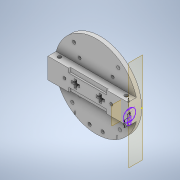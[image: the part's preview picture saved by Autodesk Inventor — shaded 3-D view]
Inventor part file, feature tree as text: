
AUTODESK INVENTOR PART (.ipt)
format: ipt  version: 2021 (Build 250183000, 183)  size: 337,920 bytes
history: native  units: mm
features: sketch x16, extrude x13, direct_edit x11, other x11, reference x9, move_body x8, plane x3, fillet x2, mirror x2
ambient origin geometry x8: Origin, YZ Plane, XZ Plane, XY Plane, X Axis, Y Axis, Z Axis, Center Point
bodies: Solid1 (feature_tree)
feature tree (75):
  sketch  "Sketch1"  dims[d0=100.0mm d1=5.0mm d2=0.0mm]
  extrude  "Extrusion1"  Depth=5.0mm TaperAngle=0.0deg
  extrude  "Extrusion2"  Depth=5.0mm
  extrude  "Extrusion3"  Depth=2.0mm
  fillet  "Fillet1"  Radius=2.0mm
  fillet  "Fillet2"  Radius=10.0mm
  extrude  "Extrusion4"  Depth=3.0mm
  extrude  "Extrusion5"  Depth=10.0mm TaperAngle=0.0deg
  plane  "Work Plane1"
  sketch  "Sketch8"  dims[d23=10.0mm d24=3.0mm]
  plane  "Work Plane3"
  extrude  "Extrusion7"  Depth=10.0mm
  plane  "Work Plane2"
  sketch  "Sketch10"  dims[d29=4.0mm d30=8.0mm]
  extrude  "Extrusion9"  Depth=3.0mm
  extrude  "Extrusion10"  Depth=3.0mm
  mirror  "Mirror3"
  extrude  "Extrusion11"  Depth=8.0mm
  extrude  "Extrusion12"  Depth=3.0mm
  extrude  "Extrusion13"  Depth=8.0mm
  direct_edit  "Direct Edit1"
  direct_edit  "Direct Edit2"
  direct_edit  "Direct Edit3"
  direct_edit  "Direct Edit4"
  direct_edit  "Direct Edit5"
  extrude  "Extrusion14"  Depth=51.75mm TaperAngle=0.0deg
  extrude  "Extrusion15"  Depth=7.0mm
  mirror  "Mirror4"
  direct_edit  "Direct Edit6"
  direct_edit  "Direct Edit7"
  direct_edit  "Direct Edit8"
  direct_edit  "Direct Edit9"
  direct_edit  "Direct Edit10"
  direct_edit  "Direct Edit11"
  sketch  "Sketch2"  dims[d3=5.0mm d4=0.0mm d5=78.0mm]
  sketch  "Sketch3"  dims[d6=3.0mm d7=0.0mm d8=2.0mm d9=2.0mm d12=10.0mm d13=0.0mm]
  reference  "Reference1"
  reference  "Reference2"
  reference  "Reference3"
  reference  "Reference4"
  sketch  "Sketch4"  dims[d15=15.0mm d17=3.0mm]
  reference  "Reference5"
  sketch  "Sketch5"  dims[d18=10.0mm d19=10.0mm d20=0.0mm]
  sketch  "Sketch6"  dims[d21=3.0mm d22=10.0mm]
  sketch  "Sketch9"  dims[d25=10.0mm d26=3.0mm]
  sketch  "Sketch11"  dims[d33=3.0mm d34=0.0mm d35=4.0mm]
  reference  "Reference6"
  reference  "Reference7"
  reference  "Reference8"
  reference  "Reference9"
  sketch  "Sketch12"  dims[d38=10.0mm d39=0.0mm d40=8.0mm]
  sketch  "Sketch13"  dims[d41=3.2mm d42=51.75mm d43=0.0mm]
  sketch  "Sketch14"  dims[d44=30.75mm d45=0.0mm d46=7.0mm]
  sketch  "Sketch15"  dims[d47=1.0mm]
  sketch  "Sketch16"  dims[d48=9.0mm]
  sketch  "Sketch17"  dims[d49=1.0mm d50=9.0mm d51=30.75mm d52=0.0mm d53=10.0mm d54=0.0mm d55=0.0mm d56=0.0mm d57=-40.0mm d58=0.0mm d59=0.0mm d60=4.75mm d61=-32.5mm d62=0.0mm d63=0.0mm d64=2.0mm d65=-2.0mm d66=5.0mm d67=5.0mm d68=2.0mm d69=0.0mm d70=85.0mm d71=33.0mm d72=4.0mm d73=4.0mm d74=28.0mm d75=0.0mm d76=0.0mm d77=1.5mm d78=0.0mm d79=0.0mm d80=1.0mm d81=0.0mm d82=-0.5mm d83=-0.5mm d84=0.0mm d85=-2.0mm d86=0.0mm d87=-2.0mm d88=0.0mm d89=0.0mm d90=2.0mm d91=0.0mm d92=0.0mm]
  parser-record x1  (decoder bookkeeping rows leaked as tree rows — omitted from the tree; the rows remain in map.json)
  other  "whole_assembly.iam"
  other  "539636 HGP-16-A-B-SSK---(asm_0_-ZH):1"
  other  "gripper extension:1"
  other  "Part3:1"
  move_body  "Move1"
  move_body  "Move2"
  move_body  "Move3"
  other  "Size1"
  other  "Delete1"
  other  "Size2"
  move_body  "Move4"
  move_body  "Move5"
  other  "Size3"
  other  "Size4"
  other  "Delete2"
  move_body  "Move6"
  move_body  "Move7"
  move_body  "Move8"
note: 1 file-system path scrubbed to <path> (originals preserved in map.json)
